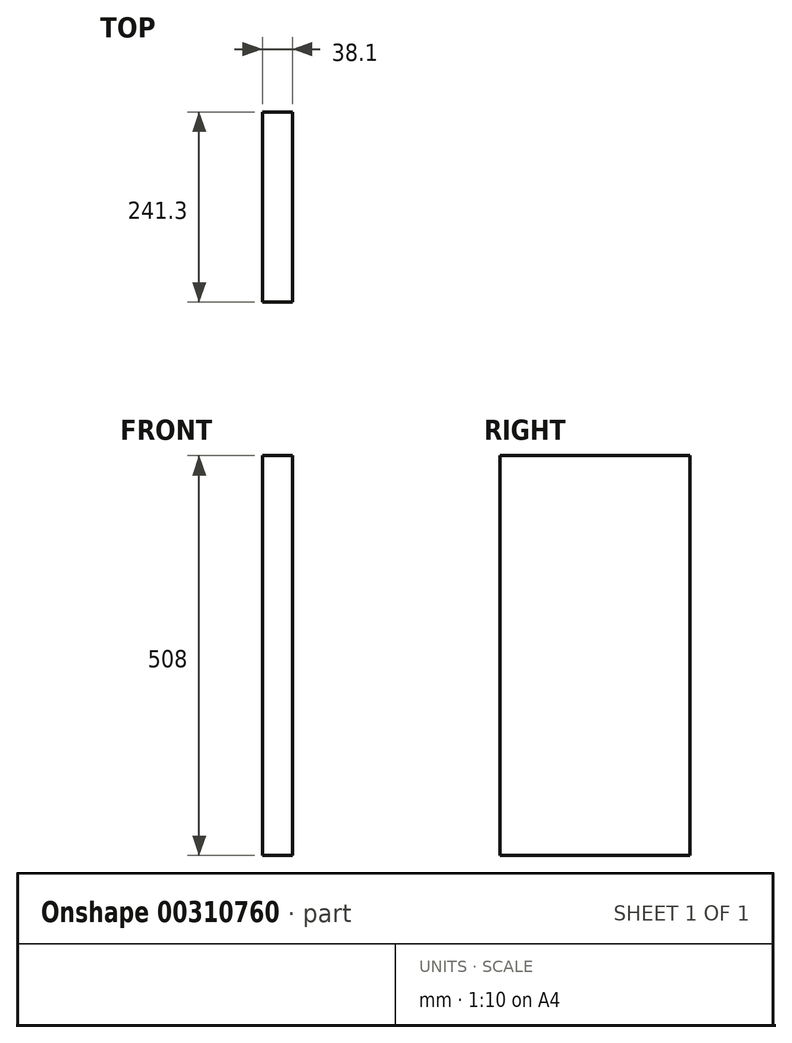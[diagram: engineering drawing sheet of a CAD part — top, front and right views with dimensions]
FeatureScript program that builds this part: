
annotation { "Feature Type Name" : "Feature", "Feature Type Description" : "" }
export const myFeature = defineFeature(function(context is Context, id is Id, definition is map)
    precondition{}
    {
        {
            var Q0;
            Q0=qCreatedBy(makeId("Top.planeOp"),FACE);
            var sketch = newSketch(context, id + "F0", { "sketchPlane" : qUnion([Q0])});
            skLineSegment(sketch, "E0.bottom", {"start": v(-65.12, -241.3) * mm, "end": v(-27.02, -241.3) * mm});
            skLineSegment(sketch, "E0.top", {"start": v(-65.12, 0) * mm, "end": v(-27.02, 0) * mm});
            skLineSegment(sketch, "E0.left", {"start": v(-65.12, -241.3) * mm, "end": v(-65.12, 0) * mm});
            skLineSegment(sketch, "E0.right", {"start": v(-27.02, -241.3) * mm, "end": v(-27.02, 0) * mm});
            skSolve(sketch);
        }
        {
            var Q0;
            Q0=makeQuery(id+"F0.imprint","IMPRINT",FACE,{"disambiguationData":[TD([[makeQuery(id+"F0.imprint","IMPRINT",EDGE,{"derivedFrom":sQuery(id+"F0.wireOp",EDGE,"E0.bottom")}),1.0]])]});
            extrude(context, id + "F1", {"entities" : qUnion([Q0]), "depth" : 508 * mm, "offsetDistance" : 25.4 * mm});
        }
    });
